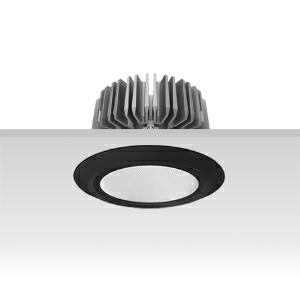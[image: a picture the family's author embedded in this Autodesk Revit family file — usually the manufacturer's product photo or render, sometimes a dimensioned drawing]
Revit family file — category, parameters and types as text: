
# Revit family: 3f_filippi_-_3f_reno_bianco_ampio_3f_filippi_-_30387_a01036_-_3f_reno_150_wh_3000-930_dali_wide___vs_bk_1c2e
name_source: partatom
category: Lighting Fixtures
units: mm (PartAtom-declared; Revit-internal decimal feet)

## family parameters
Cut with Voids When Loaded = No
Host = Face
Light Source = No
Part Type = Normal
Room Calculation Point = No
Round Connector Dimension = Use Diameter
Shared = No

## types (1)
- 3F Filippi - 3F Reno Bianco Ampio (1 x LED, 2301 lm, 37 W, 3000 K)
    Apparent Load = 37 VA
    Approval mark = CE
    CIE Flux Codes = 74 93 99 100 100
    Color Rendering = 90
    Color Temperature = 3000 K
    Control Gear = Electronic transformer
    Default Elevation = 1800 mm
    Description = ILLUMINOTECHNICAL
Luminous efficiency 100% (DLOR 100%, ULOR 0%).
Initial luminous flux of the luminaire 2301 lm.
Direct symmetric wide distribution.
Installation Interdistance Transv.D = 1.12 x hu - Long.D = 1.11 x hu.
Tabular UGR (CIE 117 - 4H-8H; S=0.25H; 70/50/20): RUG 23.9 - 23.7.
Beam angle: 74° - 73°.
Luminous efficacy 62 lm/W.
Lifetime (L90/B10): 30000 h. (tq+25°C)
Lifetime (L85/B10): 50000 h. (tq+25°C)
Lifetime (L70/B10): 80000 h. (tq+25°C)
Sudden decreased luminous flux after 50000 hours: 0% (C0).
Photobiological safety in compliance with IEC/TR 62778: RG0 risk exempt, (IEC 62471).
In compliance with IEC/EN 62722-2-1 - IEC/EN 62717 standards.

SOURCE
Compact LED module 3000/930.
Energy efficiency class (UE 2019/2020 - UE 2019/2015): F.
CIE 13.3 Colour rendering index: CRI >90 (R9 >50%).
IES TM-30 Fidelity Index: Rf = 92 Rg = 101.
CCT nominal colour temperature 3000 K.
Colour initial tolerance (MacAdam): SDCM 3.
Zhaga Book 3 compliant.

MECHANICAL
Passive heat dissipator in die-casting aluminium, oversized, for optimum thermal management of the LED module.
Parabolic element with graduated/concentric rings in white polycarbonate.
Transparent external lens with glossy and satin differentiated surfaces, with a cooling and anti-insect system in methacrylate (PMMA).
Fastening spring clips in stainless steel.
Dimensions: diameter 176 mm, height 111 mm. Weight 1.51 kg.
IP44 protection degree for exposed part, IP20 for recessed part.
Mechanical strength to impacts IK06 (1 joule).
Glow-wire test resistance 650°C.

ELECTRICAL
Wiring on a separate unit.
Halogen Free DALI-2 DATI (Parts 251, 252, 253), PUSH-DIM, electronic wiring 230V-50/60Hz, power factor 0.97 at full load, THD <25%, constant output current, SELV, class II, 1 driver, 1 DALI addresse.
Power of the luminaire 37 W.
ENEC - CE.
SAFE FLICKER: PstLM=<1 and SVM=<0.4 (IEC TR 61547-1 and IEC TR 63158), to ensure a more comfortable and safe light.
Luminaire compliant with EN 60598-2-22 for power supply from a centralised emergency system CPSS (Central Power Supply System), not incorporated in the luminaire - high risk areas excluded. The default power and flux are 100% in AC and 100% in DC.
Ambient temperature from 0°C to +25°C.
Temperature class T6 max 85°C.
Relative humidity UR: <85%.

INSTALLATION
Pull-up recessed fitting.
False ceiling carving: 150 mm.
All accessories dedicated to this product are available on the Catalog and on our website www.3F-Filippi.com.

ACCESSORIES
A01036 - Anti-glare microprismatic VS moulded glass, tempered, not flammable, locked and in line with the trim, in black polycarbonate.

APPLICATIONS
Environments: architectural, commercial, exhibition areas, transit areas, corridors, shops, display windows, service areas.
In false ceilings with narrow voids.

LIGHT MANAGEMENT
Recommended minimum setting: 10%.
The luminaire, equipped with (DALI-2 DATI) driver, can be controlled manually with 3F Easy Dim technology or automatically/manually with wired or wireless DALI/D2D control systems.
The D2D driver guarantees interoperability with other devices with the same certification by making the following information available:
Device Data (Part 251), Energy Report (Part 252), Diagnosis & Maintenance (Part 253).
In electrical systems without a regulation system (manual or automatic) and DALI bus, a suitable jumper must be made on the DA-DA terminals of the appliance.

WARNING
Luminaire designed for disposal/recycling at end-of-life.
Replaceable (LED only) light source by a professional. Replaceable control gear by a professional.
    Height = 0 mm  [stored 0 ft]
    Lamp = 1 x LED
    Lamp Light Flux = 2301 lm
    Lamp Power = 37 W
    Lamp count = 1
    Length = 176 mm
    Lifetime = 50000 h
    Luminous efficacy = 62 lm/W
    Manufacturer = 3F Filippi
    ModVariant = No
    Model = 3F Filippi - 30387+A01036 - 3F Reno 150 WH 3000-930 DALI WIDE + VS BK
    Mounting Place = Ceiling
    Mounting Type = Recessed
    Number of Poles = 1
    OnlyDefault = Yes
    Power Factor = 1
    Product Name = 3F Filippi - 3F Reno Bianco Ampio
    Product group = recessed luminaire
    ProductGroupID = 4
    Protection Class = Protection class II
    Protection Degree = IP 20
    RLX_Detail_Level = 1
    RLX_Emergency_Light_Flux = 0 lm
    RLX_Emergency_Type = 0
    RLX_Emergency_Type_DB = No
    RlxData = <blob elided: 86997 chars, md5=d748e8ab>
    Socket = socket
    Standby Power = 0 W
    System Light Flux = 2301 lm
    System Power = 37 W
    Type Comments = Product without accessories
    Type Image = 3ffilippi_3f_reno_150_bk_vs_smp.jpg
    URL = http://relux.com
    VarID = ---
    Voltage = 0 V
    Weight = 0.00 kg
    Width = 0 mm  [stored 0 ft]

note: [stored X ft] marks values corroborated as IEEE doubles in the binary element streams (Revit-internal decimal feet)

## geometry (parser evidence)
native form markers: Blend x4, Sweep x11
no freeform markers — native parametric forms only
